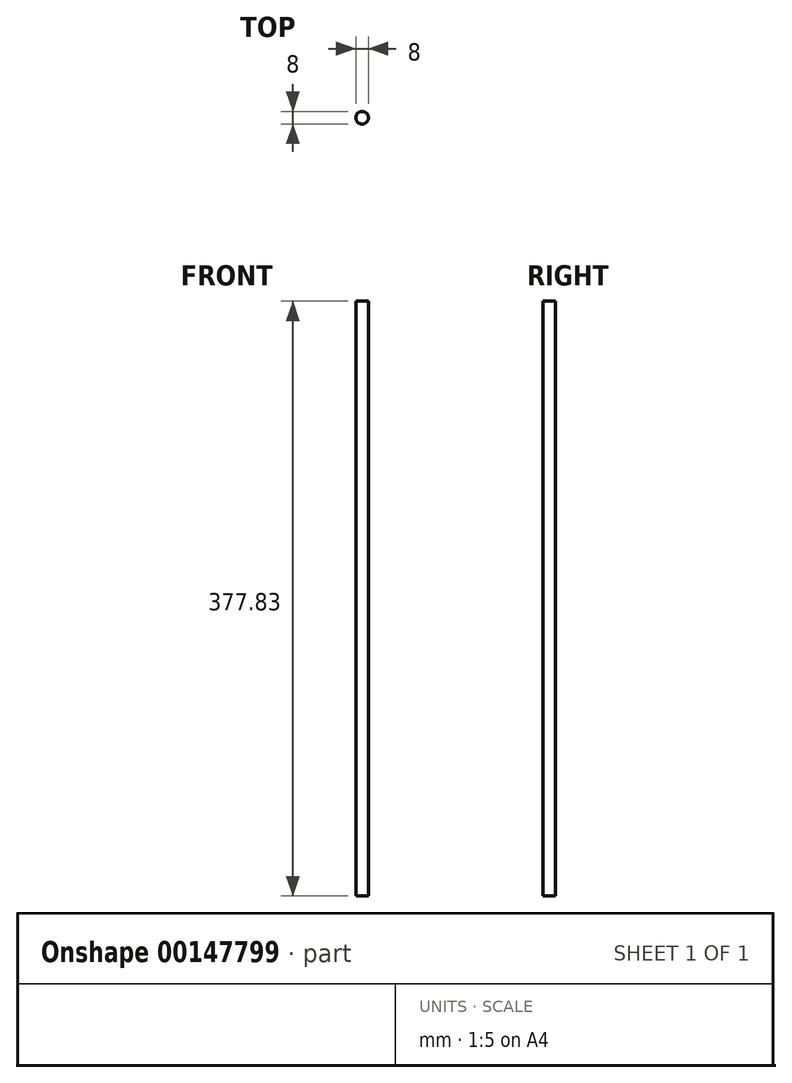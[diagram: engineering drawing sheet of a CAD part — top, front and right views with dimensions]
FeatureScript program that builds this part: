
annotation { "Feature Type Name" : "Feature", "Feature Type Description" : "" }
export const myFeature = defineFeature(function(context is Context, id is Id, definition is map)
    precondition{}
    {
        {
            var Q0;
            Q0=qCreatedBy(makeId("Top.planeOp"),FACE);
            var sketch = newSketch(context, id + "F0", { "sketchPlane" : qUnion([Q0])});
            skCircle(sketch, "E0", {"center": v(0, 0) * mm, "radius": 4 * mm});
            skSolve(sketch);
        }
        {
            var Q0;
            Q0=qSketchRegion(id+"F0",true);
            extrude(context, id + "F1", {"entities" : qUnion([Q0]), "depth" : 377.82 * mm});
        }
    });
